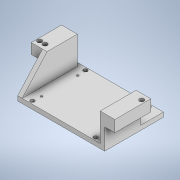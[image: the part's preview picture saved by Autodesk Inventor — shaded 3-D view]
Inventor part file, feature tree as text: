
AUTODESK INVENTOR PART (.ipt)
format: ipt  version: 2020 (Build 240168000, 168)  size: 314,880 bytes
history: native  units: mm
features: projected_geometry x13, sketch x10, extrude x7, hole x3, other x1
ambient origin geometry x8: Origin, YZ Plane, XZ Plane, XY Plane, X Axis, Y Axis, Z Axis, Center Point
bodies: Body1 (feature_tree)
feature tree (34):
  other  "솔리드1"
  extrude  "돌출1"  Depth=192.5mm
  extrude  "돌출2"  Depth=67.0mm
  extrude  "돌출3"  Depth=192.5mm
  extrude  "돌출4"  Depth=63.0mm
  hole  "구멍1"  [1 undecoded]
  extrude  "돌출5"  Depth=10.0mm
  extrude  "돌출6"  Depth=12.5mm
  hole  "구멍2"  [1 undecoded]
  extrude  "돌출7"  Depth=55.0mm
  hole  "구멍3"  [1 undecoded]
  sketch  "스케치1"
  sketch  "스케치2"
  sketch  "스케치3"
  projected_geometry  "투영된 루프1"
  sketch  "스케치5"
  projected_geometry  "투영된 루프2"
  sketch  "스케치6"
  sketch  "스케치7"
  projected_geometry  "투영된 루프3"
  sketch  "스케치8"
  projected_geometry  "투영된 루프4"
  sketch  "스케치9"
  projected_geometry  "투영된 루프5"
  projected_geometry  "투영된 루프6"
  projected_geometry  "투영된 루프7"
  projected_geometry  "투영된 루프8"
  sketch  "스케치10"
  projected_geometry  "투영된 루프9"
  sketch  "스케치11"
  projected_geometry  "투영된 루프10"
  projected_geometry  "투영된 루프11"
  projected_geometry  "투영된 루프12"
  projected_geometry  "투영된 루프13"
note: 3 required parameter values undecoded (feature->parameter linkage not recoverable at this tier; creation-order binding heuristic only, values carry confidence <= 0.55)
